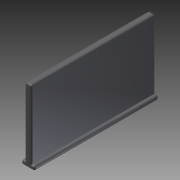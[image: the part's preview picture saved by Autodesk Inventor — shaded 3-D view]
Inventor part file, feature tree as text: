
AUTODESK INVENTOR PART (.ipt)
format: ipt  version: 2013 (Build 170138000, 138)  size: 106,496 bytes
history: native  units: in
note: dims shown in document units (in); Inventor stores cm internally (conversion verified against a paired STEP export)
features: extrude x1, fillet x1, sketch x1
ambient origin geometry x8: Origin, YZ Plane, XZ Plane, XY Plane, X Axis, Y Axis, Z Axis, Center Point
bodies: Solid1 (feature_tree)
feature tree (3):
  extrude  "Extrusion1"  Depth=0.1575in
  fillet  "Fillet1"  Radius=0.0512in
  sketch  "Sketch1"  dims[d0=0.878in d1=0.1575in d2=0.0512in d3=0.0394in d4=0.0394in d5=1.496in d6=0.0in d7=0.02in]
